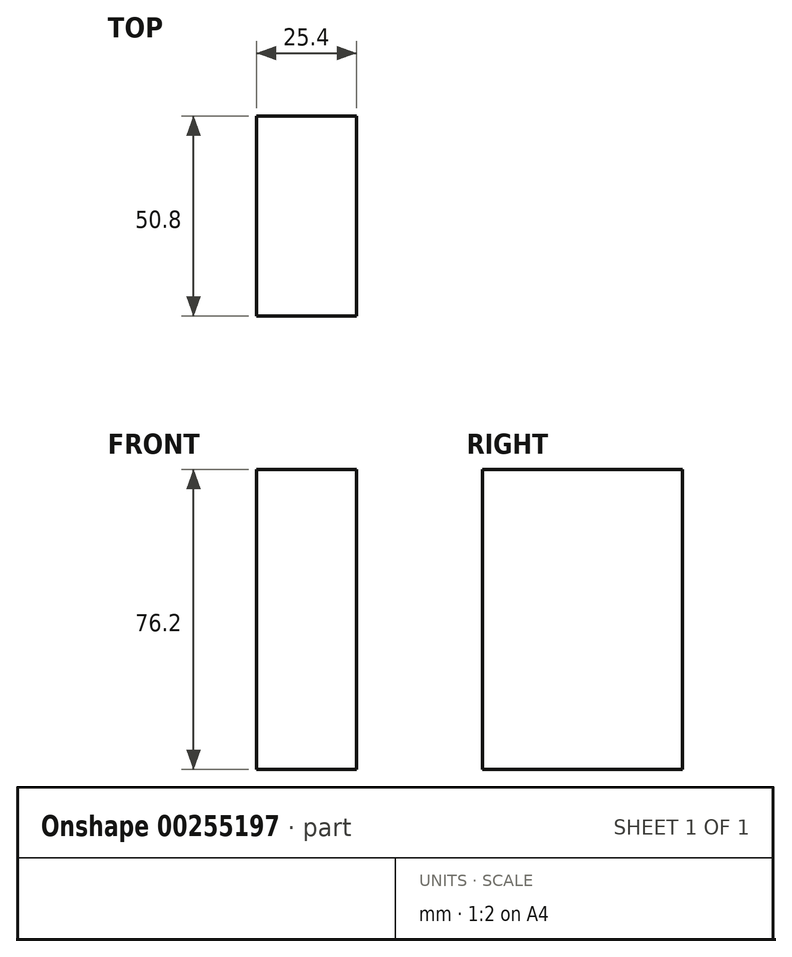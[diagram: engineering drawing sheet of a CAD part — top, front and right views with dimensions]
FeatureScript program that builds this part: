
annotation { "Feature Type Name" : "Feature", "Feature Type Description" : "" }
export const myFeature = defineFeature(function(context is Context, id is Id, definition is map)
    precondition{}
    {
        {
            var Q0;
            Q0=qCreatedBy(makeId("Right.planeOp"),FACE);
            var sketch = newSketch(context, id + "F0", { "sketchPlane" : qUnion([Q0])});
            skLineSegment(sketch, "E0.bottom", {"start": v(0.86, 0) * mm, "end": v(51.66, 0) * mm});
            skLineSegment(sketch, "E0.top", {"start": v(0.86, 76.2) * mm, "end": v(51.66, 76.2) * mm});
            skLineSegment(sketch, "E0.left", {"start": v(0.86, 0) * mm, "end": v(0.86, 76.2) * mm});
            skLineSegment(sketch, "E0.right", {"start": v(51.66, 0) * mm, "end": v(51.66, 76.2) * mm});
            skSolve(sketch);
        }
        {
            var Q0;
            Q0=makeQuery(id+"F0.imprint","IMPRINT",FACE,{"disambiguationData":[TD([[makeQuery(id+"F0.imprint","IMPRINT",EDGE,{"derivedFrom":sQuery(id+"F0.wireOp",EDGE,"E0.bottom")}),1.0]])]});
            extrude(context, id + "F1", {"entities" : qUnion([Q0]), "depth" : 25.4 * mm});
        }
    });
